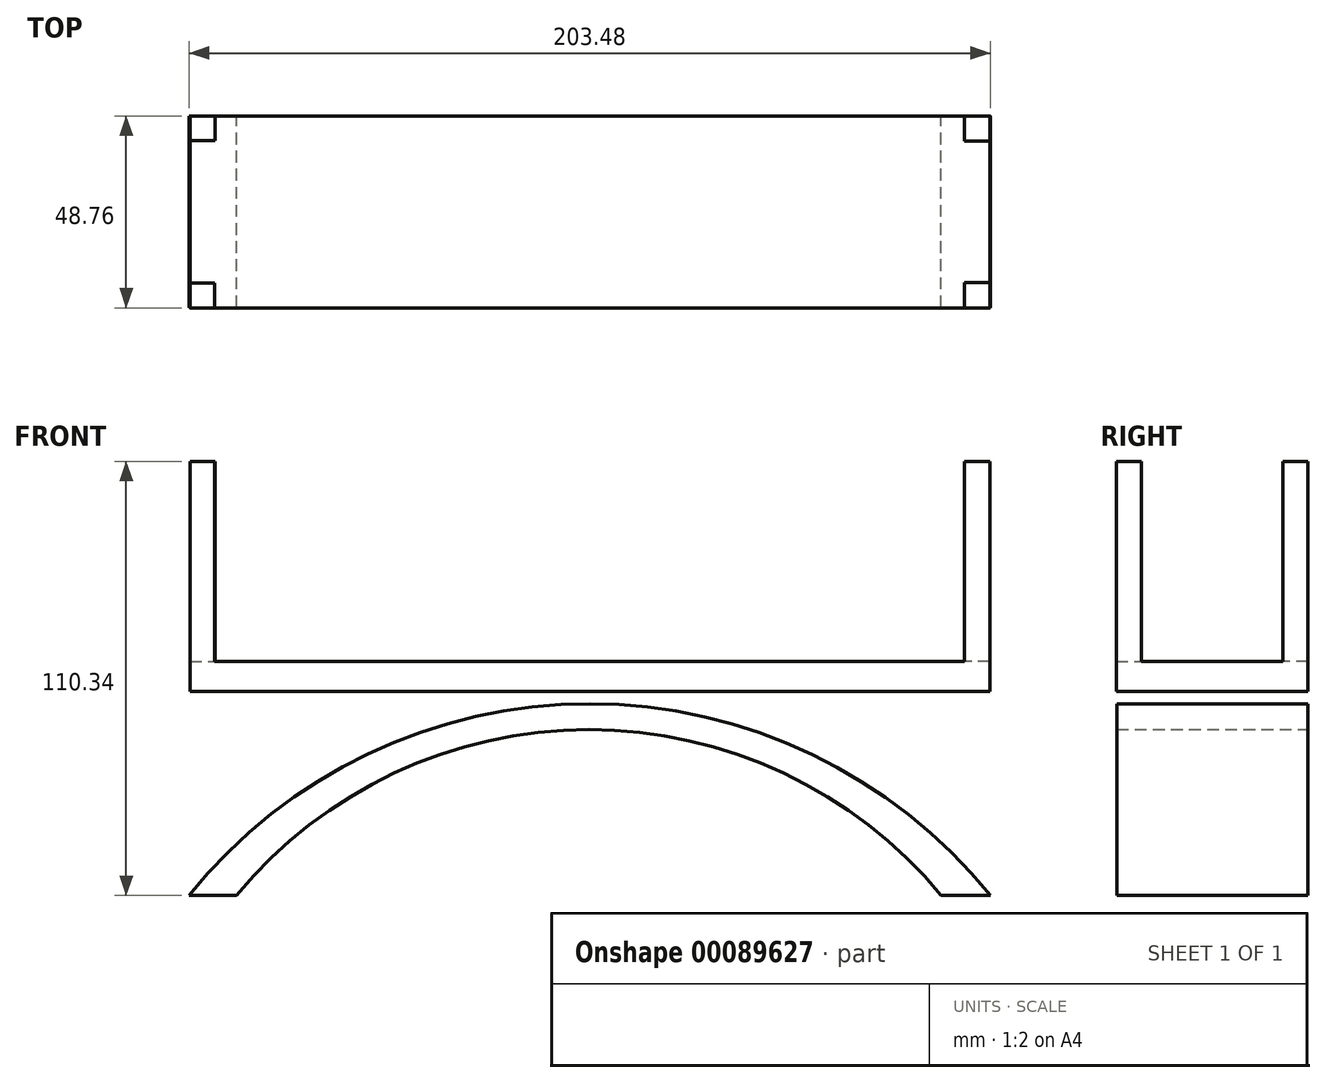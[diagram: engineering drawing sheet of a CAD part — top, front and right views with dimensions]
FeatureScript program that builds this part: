
annotation { "Feature Type Name" : "Feature", "Feature Type Description" : "" }
export const myFeature = defineFeature(function(context is Context, id is Id, definition is map)
    precondition{}
    {
        {
            var Q0;
            Q0=qCreatedBy(makeId("Front.planeOp"),FACE);
            var sketch = newSketch(context, id + "F0", { "sketchPlane" : qUnion([Q0])});
            skLineSegment(sketch, "E0.bottom", {"start": v(101.6, 3.81) * mm, "end": v(-101.6, 3.81) * mm});
            skLineSegment(sketch, "E0.top", {"start": v(101.6, -3.81) * mm, "end": v(-101.6, -3.81) * mm});
            skLineSegment(sketch, "E0.left", {"start": v(101.6, 3.81) * mm, "end": v(101.6, -3.81) * mm});
            skLineSegment(sketch, "E0.right", {"start": v(-101.6, 3.81) * mm, "end": v(-101.6, -3.81) * mm});
            skPoint(sketch, "E0.middle", {"position": v(0, 0) * mm});
            skSolve(sketch);
        }
        {
            var Q0;
            Q0=makeQuery(id+"F0.imprint","IMPRINT",FACE,{"disambiguationData":[TD([[makeQuery(id+"F0.imprint","IMPRINT",EDGE,{"derivedFrom":sQuery(id+"F0.wireOp",EDGE,"E0.bottom")}),1.0]])]});
            extrude(context, id + "F1", {"entities" : qUnion([Q0]), "depth" : 48.76 * mm});
        }
        {
            var Q0;
            Q0=makeQuery(id+"F1.opExtrude","SWEPT_FACE",FACE,{"disambiguationData":[OSD([sQuery(id+"F0.wireOp",EDGE,"E0.bottom")])]});
            var sketch = newSketch(context, id + "F2", { "sketchPlane" : qUnion([Q0])});
            skLineSegment(sketch, "E1.bottom", {"start": v(-101.6, 0) * mm, "end": v(-95.17, 0) * mm});
            skLineSegment(sketch, "E1.top", {"start": v(-101.6, -6.24) * mm, "end": v(-95.17, -6.24) * mm});
            skLineSegment(sketch, "E1.left", {"start": v(-101.6, 0) * mm, "end": v(-101.6, -6.24) * mm});
            skLineSegment(sketch, "E1.right", {"start": v(-95.17, 0) * mm, "end": v(-95.17, -6.24) * mm});
            skLineSegment(sketch, "E2.bottom", {"start": v(-101.6, -48.76) * mm, "end": v(-95.38, -48.76) * mm});
            skLineSegment(sketch, "E2.top", {"start": v(-101.6, -42.52) * mm, "end": v(-95.38, -42.52) * mm});
            skLineSegment(sketch, "E2.left", {"start": v(-101.6, -48.76) * mm, "end": v(-101.6, -42.52) * mm});
            skLineSegment(sketch, "E2.right", {"start": v(-95.38, -48.76) * mm, "end": v(-95.38, -42.52) * mm});
            skLineSegment(sketch, "E3.bottom", {"start": v(101.6, 0) * mm, "end": v(95.13, 0) * mm});
            skLineSegment(sketch, "E3.top", {"start": v(101.6, -6.44) * mm, "end": v(95.13, -6.44) * mm});
            skLineSegment(sketch, "E3.left", {"start": v(101.6, 0) * mm, "end": v(101.6, -6.44) * mm});
            skLineSegment(sketch, "E3.right", {"start": v(95.13, 0) * mm, "end": v(95.13, -6.44) * mm});
            skLineSegment(sketch, "E4.bottom", {"start": v(101.6, -48.76) * mm, "end": v(95.13, -48.76) * mm});
            skLineSegment(sketch, "E4.top", {"start": v(101.6, -42.32) * mm, "end": v(95.13, -42.32) * mm});
            skLineSegment(sketch, "E4.left", {"start": v(101.6, -48.76) * mm, "end": v(101.6, -42.32) * mm});
            skLineSegment(sketch, "E4.right", {"start": v(95.13, -48.76) * mm, "end": v(95.13, -42.32) * mm});
            skSolve(sketch);
        }
        {
            var Q0;
            Q0 = qSketchRegion(id + "F2", true);
            extrude(context, id + "F3", {"entities" : qUnion([Q0]), "operationType" : NewBodyOperationType.ADD, "depth" : 50.8 * mm});
        }
        {
            var Q0;
            Q0=qCreatedBy(makeId("Front.planeOp"),FACE);
            var sketch = newSketch(context, id + "F4", { "sketchPlane" : qUnion([Q0])});
            skArc(sketch, "E5", {"start": v(101.7, -55.73) * mm, "mid": v(0, -7) * mm, "end": v(-101.77, -55.61) * mm});
            skLineSegment(sketch, "E6", {"start": v(-101.77, -55.61) * mm, "end": v(-89.74, -55.61) * mm});
            skLineSegment(sketch, "E7", {"start": v(89.22, -55.61) * mm, "end": v(101.7, -55.73) * mm});
            skArc(sketch, "E8", {"start": v(89.22, -55.61) * mm, "mid": v(-0.26, -13.56) * mm, "end": v(-89.74, -55.61) * mm});
            skSolve(sketch);
        }
        {
            var Q0;
            Q0=makeQuery(id+"F4.imprint","IMPRINT",FACE,{"disambiguationData":[TD([[makeQuery(id+"F4.imprint","IMPRINT",EDGE,{"derivedFrom":sQuery(id+"F4.wireOp",EDGE,"E5")}),1.0]])]});
            extrude(context, id + "F5", {"entities" : qUnion([Q0]), "operationType" : NewBodyOperationType.ADD, "depth" : 48.64 * mm});
        }
        {
            var Q0;
            Q0=qCreatedBy(makeId("Front.planeOp"),FACE);
            var sketch = newSketch(context, id + "F6", { "sketchPlane" : qUnion([Q0])});
            skLineSegment(sketch, "E9", {"start": v(-101.33, -3.82) * mm, "end": v(-101.33, -55.17) * mm});
            skSolve(sketch);
        }
        {
            var Q0;
            Q0 = qSketchRegion(id + "F6", true);
            var Q1;
            Q1=sQuery(id+"F6.wireOp",EDGE,"E9");
            extrude(context, id + "F7", {"entities" : qUnion([Q0]), "bodyType" : ToolBodyType.SURFACE, "operationType" : NewBodyOperationType.ADD, "surfaceEntities" : qUnion([Q1]), "depth" : 48.73 * mm});
        }
        {
            var Q0;
            Q0=qCreatedBy(makeId("Front.planeOp"),FACE);
            var sketch = newSketch(context, id + "F8", { "sketchPlane" : qUnion([Q0])});
            skLineSegment(sketch, "E10", {"start": v(101.72, -3.53) * mm, "end": v(101.72, -55.63) * mm});
            skSolve(sketch);
        }
        {
            var Q0;
            Q0 = qSketchRegion(id + "F8", true);
            var Q1;
            Q1=sQuery(id+"F8.wireOp",EDGE,"E10");
            extrude(context, id + "F9", {"entities" : qUnion([Q0]), "bodyType" : ToolBodyType.SURFACE, "surfaceEntities" : qUnion([Q1]), "depth" : 48.07 * mm});
        }
        {
            var Q0;
            Q0=qCreatedBy(makeId("Front.planeOp"),FACE);
            var sketch = newSketch(context, id + "F10", { "sketchPlane" : qUnion([Q0])});
            skLineSegment(sketch, "E11", {"start": v(-88.16, -4.41) * mm, "end": v(-88.16, -40.95) * mm});
            skLineSegment(sketch, "E12", {"start": v(-73.73, -4.41) * mm, "end": v(-73.73, -30.55) * mm});
            skLineSegment(sketch, "E13", {"start": v(-59.3, -3.82) * mm, "end": v(-59.3, -20.82) * mm});
            skLineSegment(sketch, "E14", {"start": v(-45.54, -3.82) * mm, "end": v(-45.54, -16.45) * mm});
            skLineSegment(sketch, "E15", {"start": v(89.08, -3.86) * mm, "end": v(89.08, -42.03) * mm});
            skLineSegment(sketch, "E16", {"start": v(74.3, -3.96) * mm, "end": v(74.3, -30.26) * mm});
            skLineSegment(sketch, "E17", {"start": v(237.1, -5.3) * mm, "end": v(237.1, -37.65) * mm});
            skLineSegment(sketch, "E18", {"start": v(59.2, -3.72) * mm, "end": v(59.2, -21.49) * mm});
            skLineSegment(sketch, "E19", {"start": v(43.4, -3.97) * mm, "end": v(43.4, -14.77) * mm});
            skSolve(sketch);
        }
        {
            var Q0;
            Q0=sQuery(id+"F10.wireOp",EDGE,"E11");
            var Q1;
            Q1=sQuery(id+"F10.wireOp",EDGE,"E12");
            var Q2;
            Q2=sQuery(id+"F10.wireOp",EDGE,"E13");
            var Q3;
            Q3=sQuery(id+"F10.wireOp",EDGE,"E14");
            var Q4;
            Q4=sQuery(id+"F10.wireOp",EDGE,"E19");
            var Q5;
            Q5=sQuery(id+"F10.wireOp",EDGE,"E18");
            var Q6;
            Q6=sQuery(id+"F10.wireOp",EDGE,"E16");
            var Q7;
            Q7=sQuery(id+"F10.wireOp",EDGE,"E15");
            extrude(context, id + "F11", {"bodyType" : ToolBodyType.SURFACE, "surfaceEntities" : qUnion([Q0, Q1, Q2, Q3, Q4, Q5, Q6, Q7]), "depth" : 48.62 * mm});
        }
        {
            var Q0;
            Q0=makeQuery(id+"F1.opExtrude","SWEPT_FACE",FACE,{"disambiguationData":[OSD([sQuery(id+"F0.wireOp",EDGE,"E0.bottom")])]});
            var sketch = newSketch(context, id + "F12", { "sketchPlane" : qUnion([Q0])});
            skLineSegment(sketch, "E20", {"start": v(-101.6, -24.38) * mm, "end": v(101.6, -24.38) * mm});
            skSolve(sketch);
        }
        {
            var Q0;
            Q0 = qSketchRegion(id + "F12", true);
            var Q1;
            Q1=sQuery(id+"F12.wireOp",EDGE,"E20");
            extrude(context, id + "F13", {"entities" : qUnion([Q0]), "bodyType" : ToolBodyType.SURFACE, "surfaceEntities" : qUnion([Q1]), "depth" : 1.84 * mm});
        }
    });
